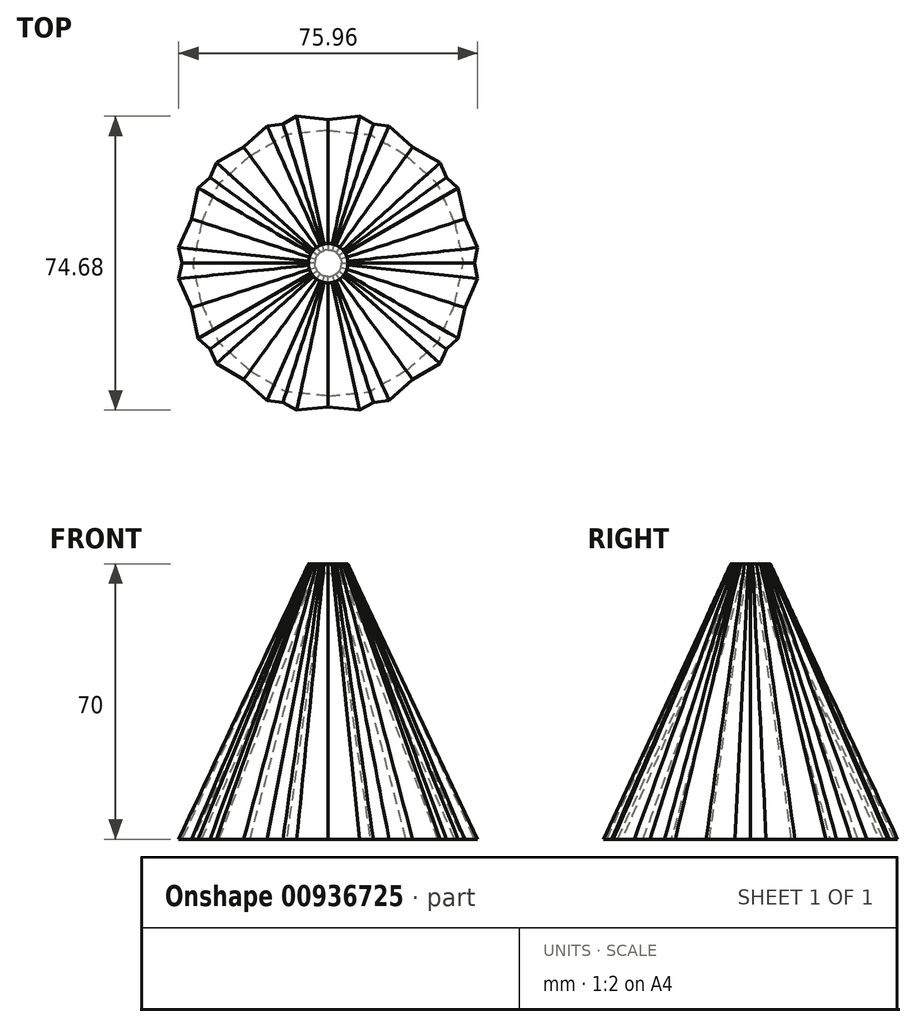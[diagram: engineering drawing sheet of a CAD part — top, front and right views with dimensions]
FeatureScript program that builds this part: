
annotation { "Feature Type Name" : "Feature", "Feature Type Description" : "" }
export const myFeature = defineFeature(function(context is Context, id is Id, definition is map)
    precondition{}
    {
        {
            var Q0;
            Q0=qCreatedBy(makeId("Top.planeOp"),FACE);
            var sketch = newSketch(context, id + "F0", { "sketchPlane" : qUnion([Q0])});
            skCircle(sketch, "E0.cCircle", {"center": v(0, 0) * mm, "radius": 36.32 * mm, "construction": true});
            skLineSegment(sketch, "E0.0", {"start": v(-33.05, -19.13) * mm, "end": v(-37.98, 3.95) * mm});
            skLineSegment(sketch, "E0.1", {"start": v(-37.98, 3.95) * mm, "end": v(-28.41, 25.52) * mm});
            skLineSegment(sketch, "E0.2", {"start": v(-28.41, 25.52) * mm, "end": v(-7.98, 37.34) * mm});
            skLineSegment(sketch, "E0.3", {"start": v(-7.98, 37.34) * mm, "end": v(15.5, 34.9) * mm});
            skLineSegment(sketch, "E0.4", {"start": v(15.5, 34.9) * mm, "end": v(33.05, 19.13) * mm});
            skLineSegment(sketch, "E0.5", {"start": v(33.05, 19.13) * mm, "end": v(37.98, -3.95) * mm});
            skLineSegment(sketch, "E0.6", {"start": v(37.98, -3.95) * mm, "end": v(28.41, -25.52) * mm});
            skLineSegment(sketch, "E0.7", {"start": v(28.41, -25.52) * mm, "end": v(7.98, -37.34) * mm});
            skLineSegment(sketch, "E0.8", {"start": v(7.98, -37.34) * mm, "end": v(-15.5, -34.9) * mm});
            skLineSegment(sketch, "E0.9", {"start": v(-15.5, -34.9) * mm, "end": v(-33.05, -19.13) * mm});
            skPoint(sketch, "E0.0.midPoint", {"position": v(-35.52, -7.6) * mm});
            skSolve(sketch);
        }
        {
            var Q0;
            Q0=qCreatedBy(makeId("Top.planeOp"),FACE);
            cPlane(context, id + "F1", {"entities" : qUnion([Q0]), "cplaneType" : CPlaneType.OFFSET, "offset" : 70 * mm, "width" : 150 * mm, "height" : 150 * mm});
        }
        {
            var Q0;
            Q0=qCreatedBy(id+"F1.planeOp",FACE);
            var sketch = newSketch(context, id + "F2", { "sketchPlane" : qUnion([Q0])});
            skCircle(sketch, "E1", {"center": v(0, 0) * mm, "radius": 5 * mm});
            skSolve(sketch);
        }
        {
            var Q0;
            Q0=makeQuery(id+"F2.imprint","IMPRINT",FACE,{"disambiguationData":[TD([[makeQuery(id+"F2.imprint","IMPRINT",EDGE,{"derivedFrom":sQuery(id+"F2.wireOp",EDGE,"E1")}),1.0]])]});
            var Q1;
            Q1=makeQuery(id+"F0.imprint","IMPRINT",FACE,{"disambiguationData":[TD([[makeQuery(id+"F0.imprint","IMPRINT",EDGE,{"derivedFrom":sQuery(id+"F0.wireOp",EDGE,"E0.0")}),-1.0]])]});
            loft(context, id + "F3", {"sheetProfilesArray" : [{ "sheetProfileEntities" : qUnion([Q0]) }, { "sheetProfileEntities" : qUnion([Q1]) }]});
        }
        {
            var Q0;
            Q0=makeQuery(id+"F3.opLoft","CAP_FACE",FACE,{"disambiguationData":[OSD([makeQuery(id+"F0.imprint","IMPRINT",FACE,{"disambiguationData":[TD([[makeQuery(id+"F0.imprint","IMPRINT",EDGE,{"derivedFrom":sQuery(id+"F0.wireOp",EDGE,"E0.0")}),-1.0]])]})])],"isStart":true});
            shell(context, id + "F4", {"entities" : qUnion([Q0]), "thickness" : 2.5 * mm});
        }
        {
            var Q0;
            Q0=makeQuery(id+"F3.opLoft","SWEPT_BODY",BODY,{"disambiguationData":[OSD([makeQuery(id+"F0.imprint","IMPRINT",FACE,{"disambiguationData":[TD([[makeQuery(id+"F0.imprint","IMPRINT",EDGE,{"derivedFrom":sQuery(id+"F0.wireOp",EDGE,"E0.0")}),-1.0]])]}),makeQuery(id+"F2.imprint","IMPRINT",FACE,{"disambiguationData":[TD([[makeQuery(id+"F2.imprint","IMPRINT",EDGE,{"derivedFrom":sQuery(id+"F2.wireOp",EDGE,"E1")}),1.0]])]})])]});
            var Q1;
            Q1=qCreatedBy(makeId("Right.planeOp"),FACE);
            mirror(context, id + "F5", {"operationType" : NewBodyOperationType.ADD, "entities" : qUnion([Q0]), "mirrorPlane" : qUnion([Q1])});
        }
    });
